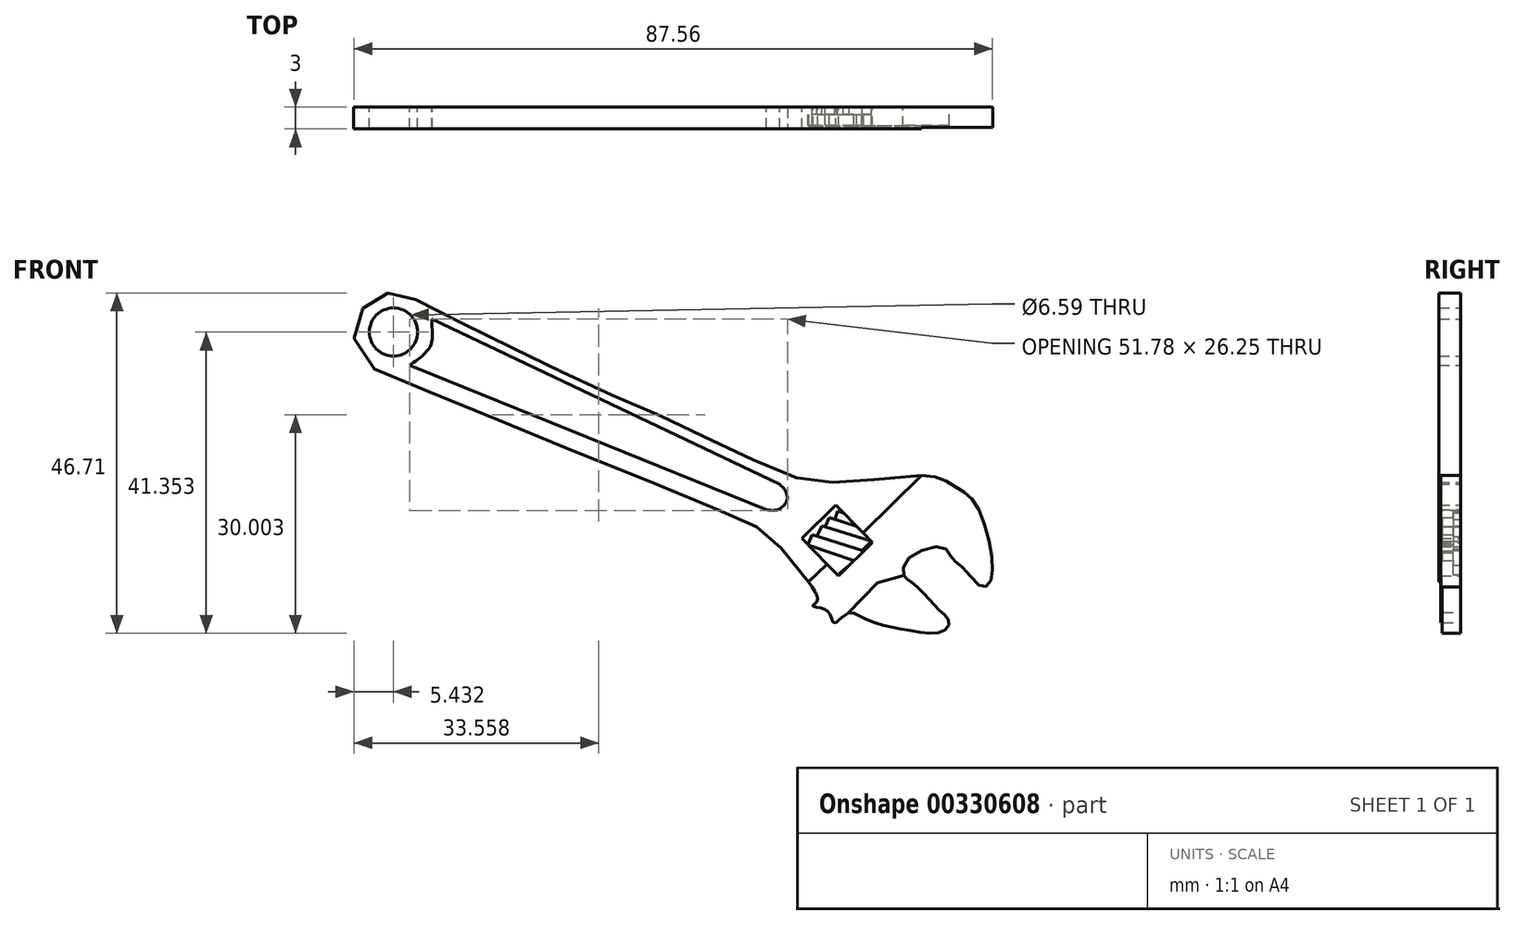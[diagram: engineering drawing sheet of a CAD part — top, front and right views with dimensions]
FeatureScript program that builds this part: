
annotation { "Feature Type Name" : "Feature", "Feature Type Description" : "" }
export const myFeature = defineFeature(function(context is Context, id is Id, definition is map)
    precondition{}
    {
        {
            var Q0;
            Q0=qCreatedBy(makeId("Front.planeOp"),FACE);
            var sketch = newSketch(context, id + "F0", { "sketchPlane" : qUnion([Q0])});
            skCircle(sketch, "E0", {"center": v(-27.24, 25.71) * mm, "radius": 3.3 * mm});
            skFitSpline(sketch, "E1", {"points": [v(-32.18, 27.8) * mm, v(-32.64, 24.86) * mm, v(-31.1, 21.55) * mm, v(-24.15, 18.23) * mm, v(-8.87, 11.98) * mm, v(8.49, 4.96) * mm, v(20.37, 0) * mm, v(23, -1.3) * mm, v(25.54, -3.45) * mm, v(27.32, -5.85) * mm, v(30.87, -11.1) * mm, v(30.25, -11.87) * mm, v(32.26, -12.56) * mm, v(33.18, -14.18) * mm, v(35.03, -12.87) * mm, v(36.65, -13.25) * mm, v(40.13, -14.57) * mm, v(44.14, -15.34) * mm, v(48, -15.42) * mm, v(48.92, -14.03) * mm, v(47.69, -12.56) * mm, v(45.91, -10.63) * mm, v(43.6, -8.47) * mm, v(42.75, -7.7) * mm, v(43.3, -5.46) * mm, v(48.15, -3.84) * mm, v(49.3, -5.3) * mm, v(50.78, -6.54) * mm, v(53.48, -9.24) * mm, v(54.56, -8.55) * mm, v(54.71, -4.61) * mm, v(52.47, 2.26) * mm, v(50.16, 4.26) * mm, v(46.84, 5.88) * mm, v(40.74, 5.65) * mm, v(35.19, 5.26) * mm, v(30.94, 5.11) * mm, v(27.16, 6.04) * mm, v(20.76, 8.74) * mm, v(13.2, 12.36) * mm, v(7.8, 14.91) * mm, v(0, 18.23) * mm, v(-7.8, 22) * mm, v(-15.59, 25.8) * mm, v(-23.46, 29.8) * mm, v(-26.08, 30.88) * mm, v(-28.31, 31) * mm, v(-30.4, 29.96) * mm, v(-32.18, 27.8) * mm]});
            skLineSegment(sketch, "E2", {"start": v(28.78, -2.6) * mm, "end": v(33.41, 1.95) * mm});
            skLineSegment(sketch, "E3", {"start": v(33.41, 1.95) * mm, "end": v(38.42, -3.15) * mm});
            skLineSegment(sketch, "E4", {"start": v(38.42, -3.15) * mm, "end": v(33.75, -7.74) * mm});
            skLineSegment(sketch, "E5", {"start": v(33.75, -7.74) * mm, "end": v(28.78, -2.6) * mm});
            skLineSegment(sketch, "E6", {"start": v(-22, 27.49) * mm, "end": v(25.7, 4.8) * mm});
            skLineSegment(sketch, "E7", {"start": v(-25, 21.16) * mm, "end": v(23.85, 1.33) * mm});
            skFitSpline(sketch, "E8", {"points": [v(-25, 21.16) * mm, v(-23.53, 22.24) * mm, v(-22.15, 23.86) * mm, v(-21.91, 25.33) * mm, v(-22, 27.49) * mm], "startDerivative": vector(5.88, 3.98) * mm, "endDerivative": vector(-0.4, 8.5) * mm});
            skFitSpline(sketch, "E9", {"points": [v(23.85, 1.33) * mm, v(25.39, 1.33) * mm, v(26.47, 2.18) * mm, v(26.78, 3.03) * mm, v(26.31, 4.18) * mm, v(25.7, 4.8) * mm], "startDerivative": vector(7.02, -1.04) * mm, "endDerivative": vector(-3.67, 3.02) * mm});
            skLineSegment(sketch, "E10", {"start": v(35.03, -12.87) * mm, "end": v(39.1, -8.7) * mm});
            skLineSegment(sketch, "E11", {"start": v(39.1, -8.7) * mm, "end": v(42.75, -7.7) * mm});
            skLineSegment(sketch, "E12", {"start": v(29.64, -8.6) * mm, "end": v(32.26, -6.06) * mm});
            skLineSegment(sketch, "E13", {"start": v(37.14, -1.84) * mm, "end": v(45.14, 6.03) * mm});
            skLineSegment(sketch, "E14", {"start": v(45.14, 6.03) * mm, "end": v(45.56, 5.85) * mm});
            skSolve(sketch);
        }
        {
            var Q0;
            Q0=makeQuery(id+"F0.imprint","IMPRINT",FACE,{"disambiguationData":[TD([[makeQuery(id+"F0.imprint","IMPRINT",EDGE,{"derivedFrom":sQuery(id+"F0.wireOp",EDGE,"E0")}),-1.0]])]});
            extrude(context, id + "F1", {"entities" : qUnion([Q0]), "depth" : 3 * mm});
        }
        {
            var Q0;
            {var subQ0=sQuery(id+"F0.wireOp",EDGE,"E4");Q0=makeQuery(id+"F0.imprint","IMPRINT",FACE,{"disambiguationData":[TD([[makeQuery(id+"F0.imprint","IMPRINT",EDGE,{"derivedFrom":subQ0}),1.0]])]});}
            extrude(context, id + "F2", {"entities" : qUnion([Q0]), "operationType" : NewBodyOperationType.ADD, "depth" : 2.75 * mm});
        }
        {
            var Q0;
            {var subQ0=sQuery(id+"F0.wireOp",EDGE,"E10");Q0=makeQuery(id+"F0.imprint","IMPRINT",FACE,{"disambiguationData":[TD([[makeQuery(id+"F0.imprint","IMPRINT",EDGE,{"derivedFrom":subQ0}),-1.0]])]});}
            extrude(context, id + "F3", {"entities" : qUnion([Q0]), "operationType" : NewBodyOperationType.ADD, "depth" : 2.5 * mm});
        }
        {
            var Q0;
            {var subQ3=sQuery(id+"F0.wireOp",EDGE,"E2");Q0=makeQuery(id+"F0.imprint","IMPRINT",FACE,{"disambiguationData":[TD([[makeQuery(id+"F0.imprint","IMPRINT",EDGE,{"derivedFrom":subQ3}),-1.0]])]});}
            var sketch = newSketch(context, id + "F4", { "sketchPlane" : qUnion([Q0])});
            skLineSegment(sketch, "E15", {"start": v(29.54, -3.5) * mm, "end": v(30.17, -2.12) * mm});
            skLineSegment(sketch, "E16", {"start": v(30.17, -2.12) * mm, "end": v(37.2, -4.33) * mm});
            skLineSegment(sketch, "E17", {"start": v(37.2, -4.33) * mm, "end": v(35.97, -5.67) * mm});
            skLineSegment(sketch, "E18", {"start": v(35.97, -5.67) * mm, "end": v(29.54, -3.5) * mm});
            skLineSegment(sketch, "E19", {"start": v(30.8, -2.31) * mm, "end": v(31.47, -0.86) * mm});
            skLineSegment(sketch, "E20", {"start": v(31.47, -0.86) * mm, "end": v(38.28, -3) * mm});
            skLineSegment(sketch, "E21", {"start": v(38.28, -3) * mm, "end": v(37, -4.27) * mm});
            skLineSegment(sketch, "E22", {"start": v(31.96, -1.01) * mm, "end": v(32.53, 0.24) * mm});
            skLineSegment(sketch, "E23", {"start": v(32.53, 0.24) * mm, "end": v(38.28, -1.58) * mm});
            skLineSegment(sketch, "E24", {"start": v(38.28, -1.58) * mm, "end": v(38.28, -3) * mm});
            skLineSegment(sketch, "E25", {"start": v(33.28, 0) * mm, "end": v(33.64, 1.16) * mm});
            skLineSegment(sketch, "E26", {"start": v(33.64, 1.16) * mm, "end": v(37.93, -0.19) * mm});
            skLineSegment(sketch, "E27", {"start": v(37.93, -0.19) * mm, "end": v(38.28, -1.58) * mm});
            skLineSegment(sketch, "E28", {"start": v(30.17, -3.72) * mm, "end": v(30.17, -5.67) * mm});
            skLineSegment(sketch, "E29", {"start": v(30.17, -5.67) * mm, "end": v(33.64, -7.59) * mm});
            skLineSegment(sketch, "E30", {"start": v(33.64, -7.59) * mm, "end": v(35.97, -5.67) * mm});
            skSolve(sketch);
        }
        {
            var Q0;
            {var subQ1=sQuery(id+"F4.wireOp",EDGE,"E16");var subQ9=sQuery(id+"F4.wireOp",EDGE,"E15");var subQ10=makeQuery(id+"F4.imprint","INTERSECT",VERTEX,{"derivedFrom":[subQ9,subQ1]});Q0=makeQuery(id+"F4.imprint","IMPRINT",FACE,{"disambiguationData":[TD([[makeQuery(id+"F4.imprint","IMPRINT",EDGE,{"disambiguationData":[TD([[subQ10,-1.0]])],"derivedFrom":subQ1}),-1.0]])]});}
            var Q1;
            {var subQ6=sQuery(id+"F4.wireOp",EDGE,"E22");Q1=makeQuery(id+"F4.imprint","IMPRINT",FACE,{"disambiguationData":[TD([[makeQuery(id+"F4.imprint","IMPRINT",EDGE,{"derivedFrom":subQ6}),-1.0]])]});}
            extrude(context, id + "F5", {"entities" : qUnion([Q0, Q1]), "operationType" : NewBodyOperationType.ADD, "depth" : 2.5 * mm});
        }
        {
            var Q0;
            {var subQ1=sQuery(id+"F4.wireOp",EDGE,"E19");Q0=makeQuery(id+"F4.imprint","IMPRINT",FACE,{"disambiguationData":[TD([[makeQuery(id+"F4.imprint","IMPRINT",EDGE,{"derivedFrom":subQ1}),-1.0]])]});}
            var Q1;
            {var subQ0=sQuery(id+"F4.wireOp",EDGE,"E25");Q1=makeQuery(id+"F4.imprint","IMPRINT",FACE,{"disambiguationData":[TD([[makeQuery(id+"F4.imprint","IMPRINT",EDGE,{"derivedFrom":subQ0}),-1.0]])]});}
            var Q2;
            {var subQ6=sQuery(id+"F4.wireOp",EDGE,"E28");var subQ7=sQuery(id+"F4.wireOp",EDGE,"E18");var subQ8=makeQuery(id+"F4.imprint","INTERSECT",VERTEX,{"derivedFrom":[subQ7,subQ6]});Q2=makeQuery(id+"F4.imprint","IMPRINT",FACE,{"disambiguationData":[TD([[makeQuery(id+"F4.imprint","IMPRINT",EDGE,{"disambiguationData":[TD([[subQ8,1.0]])],"derivedFrom":subQ7}),1.0]])]});}
            extrude(context, id + "F6", {"entities" : qUnion([Q0, Q1, Q2]), "operationType" : NewBodyOperationType.ADD, "depth" : 1 * mm});
        }
    });
